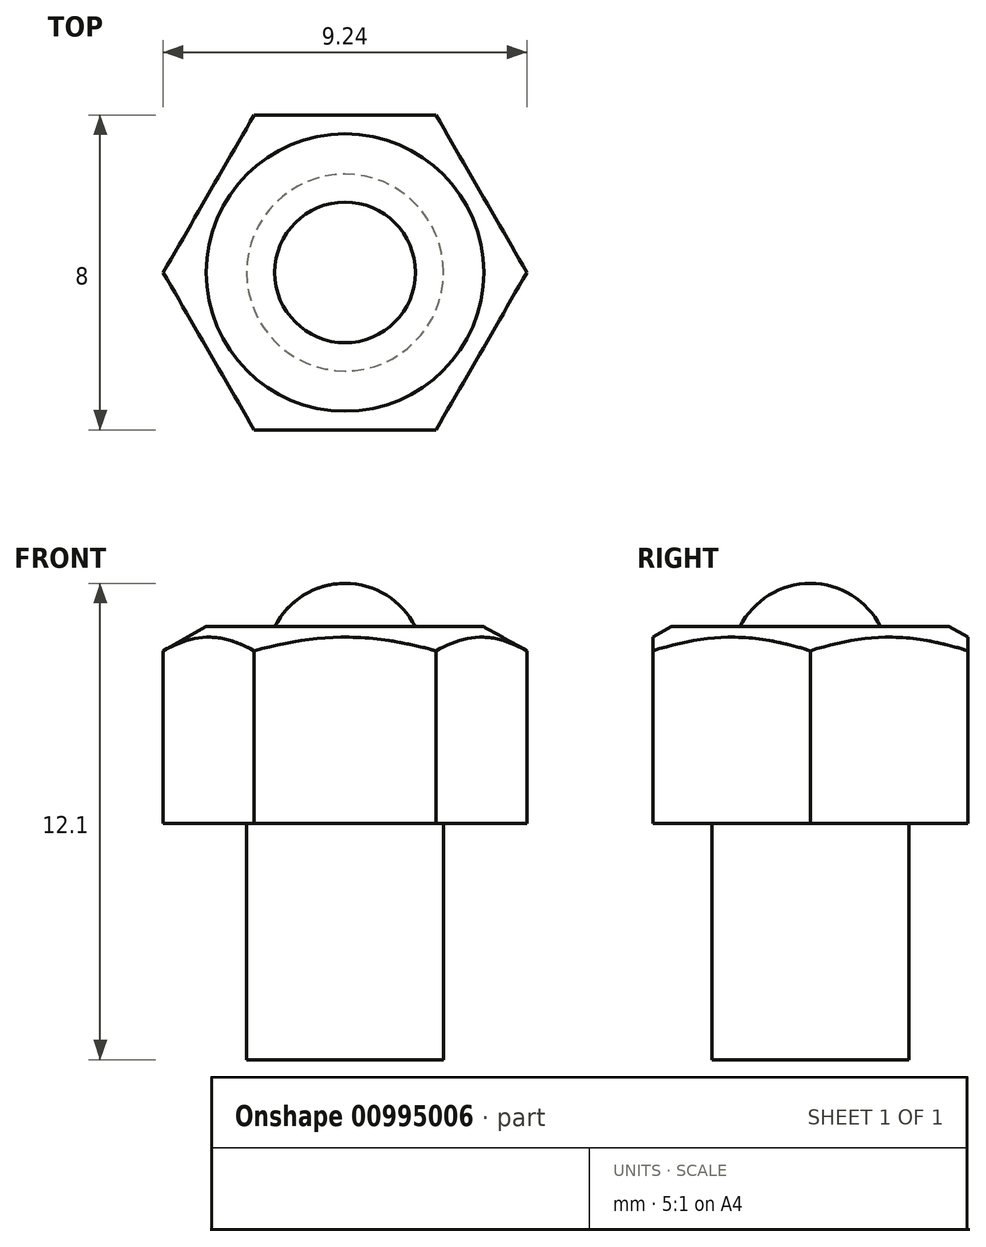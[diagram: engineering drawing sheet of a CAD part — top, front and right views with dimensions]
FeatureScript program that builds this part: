
annotation { "Feature Type Name" : "Feature", "Feature Type Description" : "" }
export const myFeature = defineFeature(function(context is Context, id is Id, definition is map)
    precondition{}
    {
        {
            var Q0;
            Q0=qCreatedBy(makeId("Top.planeOp"),FACE);
            var sketch = newSketch(context, id + "F0", { "sketchPlane" : qUnion([Q0])});
            skCircle(sketch, "E0.cCircle", {"center": v(0, 0) * mm, "radius": 4 * mm, "construction": true});
            skLineSegment(sketch, "E0.0", {"start": v(-2.3, 4) * mm, "end": v(2.3, 4) * mm});
            skLineSegment(sketch, "E0.1", {"start": v(2.3, 4) * mm, "end": v(4.62, 0) * mm});
            skLineSegment(sketch, "E0.2", {"start": v(4.62, 0) * mm, "end": v(2.3, -4) * mm});
            skLineSegment(sketch, "E0.3", {"start": v(2.3, -4) * mm, "end": v(-2.3, -4) * mm});
            skLineSegment(sketch, "E0.4", {"start": v(-2.3, -4) * mm, "end": v(-4.62, 0) * mm});
            skLineSegment(sketch, "E0.5", {"start": v(-4.62, 0) * mm, "end": v(-2.3, 4) * mm});
            skPoint(sketch, "E0.0.midPoint", {"position": v(0, 4) * mm});
            skSolve(sketch);
        }
        {
            var Q0;
            Q0=qSketchRegion(id+"F0",true);
            extrude(context, id + "F1", {"entities" : qUnion([Q0]), "depth" : 5 * mm, "offsetDistance" : 25 * mm});
        }
        {
            var Q0;
            Q0=makeQuery(id+"F1.opExtrude","CAP_FACE",FACE,{"disambiguationData":[OSD([sQuery(id+"F0.wireOp",EDGE,"E0.0"),sQuery(id+"F0.wireOp",EDGE,"E0.1"),sQuery(id+"F0.wireOp",EDGE,"E0.2"),sQuery(id+"F0.wireOp",EDGE,"E0.3"),sQuery(id+"F0.wireOp",EDGE,"E0.4"),sQuery(id+"F0.wireOp",EDGE,"E0.5")])],"isStart":true});
            var sketch = newSketch(context, id + "F2", { "sketchPlane" : qUnion([Q0])});
            skCircle(sketch, "E1", {"center": v(0, 0) * mm, "radius": 2.5 * mm});
            skSolve(sketch);
        }
        {
            var Q0;
            Q0=qSketchRegion(id+"F2",true);
            extrude(context, id + "F3", {"entities" : qUnion([Q0]), "operationType" : NewBodyOperationType.ADD, "depth" : 6 * mm, "offsetDistance" : 25 * mm});
        }
        {
            var Q0;
            Q0=qCreatedBy(makeId("Front.planeOp"),FACE);
            var sketch = newSketch(context, id + "F4", { "sketchPlane" : qUnion([Q0])});
            skLineSegment(sketch, "E2", {"start": v(1.24, 6.28) * mm, "end": v(5.27, 4.02) * mm});
            skLineSegment(sketch, "E3", {"start": v(5.27, 4.02) * mm, "end": v(5.27, 6.98) * mm});
            skLineSegment(sketch, "E4", {"start": v(5.27, 6.98) * mm, "end": v(1.24, 6.98) * mm});
            skLineSegment(sketch, "E5", {"start": v(0, 8.17) * mm, "end": v(0, 5.7) * mm});
            skLineSegment(sketch, "E6", {"start": v(1.24, 6.98) * mm, "end": v(1.24, 6.28) * mm});
            skPoint(sketch, "E7.orphan", {"position": v(0, 6.98) * mm});
            skSolve(sketch);
        }
        {
            var Q0;
            Q0=makeQuery(id+"F4.imprint","IMPRINT",FACE,{"disambiguationData":[TD([[makeQuery(id+"F4.imprint","IMPRINT",EDGE,{"derivedFrom":sQuery(id+"F4.wireOp",EDGE,"E2")}),1.0]])]});
            var Q1;
            Q1=sQuery(id+"F4.wireOp",EDGE,"E5");
            revolve(context, id + "F5", {"operationType" : NewBodyOperationType.REMOVE, "surfaceOperationType" : NewSurfaceOperationType.NEW, "entities" : qUnion([Q0]), "axis" : qUnion([Q1]), "revolveType" : RevolveType.FULL, "oppositeDirection" : true});
        }
        {
            var Q0;
            Q0=qCreatedBy(makeId("Front.planeOp"),FACE);
            var sketch = newSketch(context, id + "F6", { "sketchPlane" : qUnion([Q0])});
            skArc(sketch, "E8", {"start": v(0, 2.1) * mm, "mid": v(2, 4.1) * mm, "end": v(0, 6.1) * mm});
            skLineSegment(sketch, "E9", {"start": v(0, 6.1) * mm, "end": v(0, 2.1) * mm});
            skSolve(sketch);
        }
        {
            var Q0;
            Q0=qSketchRegion(id+"F6",true);
            var Q1;
            Q1=sQuery(id+"F6.wireOp",EDGE,"E9");
            revolve(context, id + "F7", {"operationType" : NewBodyOperationType.ADD, "surfaceOperationType" : NewSurfaceOperationType.NEW, "entities" : qUnion([Q0]), "axis" : qUnion([Q1]), "revolveType" : RevolveType.FULL});
        }
    });
